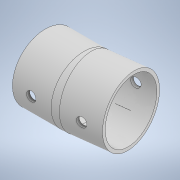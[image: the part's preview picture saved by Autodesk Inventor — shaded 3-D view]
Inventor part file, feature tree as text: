
AUTODESK INVENTOR PART (.ipt)
format: ipt  version: 2022 (Build 260153000, 153)  size: 244,224 bytes
history: native  units: mm
features: sketch x4, extrude x2, sweep x1
ambient origin geometry x8: Origin, YZ Plane, XZ Plane, XY Plane, X Axis, Y Axis, Z Axis, Center Point
bodies: Body1 (feature_tree)
feature tree (7):
  sweep  "Sweep1"
  extrude  "Extrusion8"  Depth=30.194196mm
  extrude  "Extrusion9"  Depth=10.0mm
  sketch  "Sketch5"  dims[d31=34.456mm d122=13.0mm]
  sketch  "Sketch6"  dims[d123=13.0mm d124=30.194196mm]
  sketch  "Sketch7"  dims[d125=10.0mm d126=19.0mm]
  sketch  "Sketch8"  dims[d127=21.0mm d128=0.0mm d129=0.0mm d130=6.0mm d131=3.0mm d132=25.0mm d133=0.0mm d134=6.0mm d135=3.0mm d136=25.0mm d137=0.0mm d138=0.01mm d139=0.01mm]
